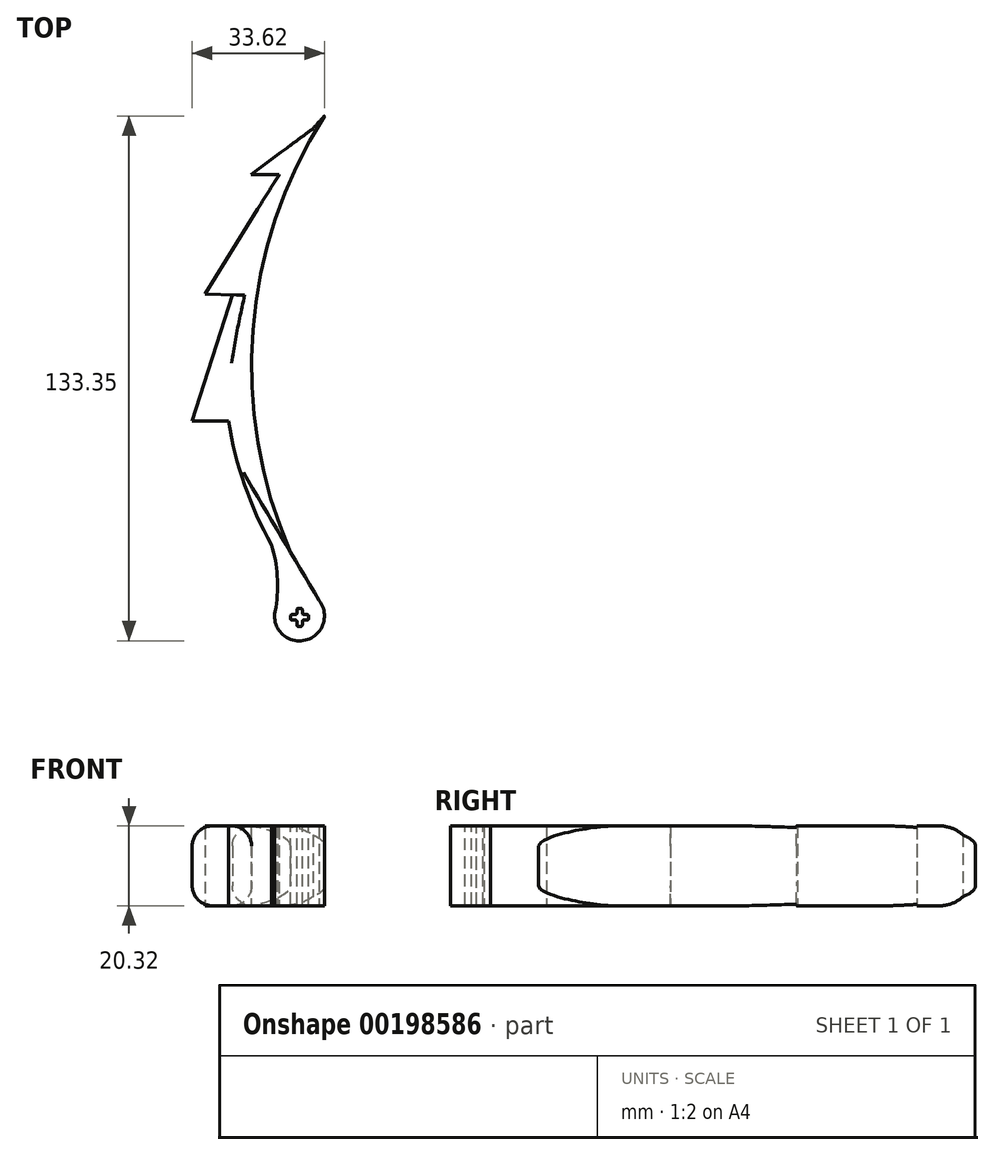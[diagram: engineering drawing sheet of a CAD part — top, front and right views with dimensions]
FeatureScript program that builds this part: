
annotation { "Feature Type Name" : "Feature", "Feature Type Description" : "" }
export const myFeature = defineFeature(function(context is Context, id is Id, definition is map)
    precondition{}
    {
        {
            var Q0;
            Q0=qCreatedBy(makeId("Top.planeOp"),FACE);
            var sketch = newSketch(context, id + "F0", { "sketchPlane" : qUnion([Q0])});
            skPoint(sketch, "E0.middle", {"position": v(0, 0) * mm});
            skPoint(sketch, "E1", {"position": v(0, -63.5) * mm});
            skArc(sketch, "E2", {"start": v(12.7, 63.5) * mm, "mid": v(11.22, 61.91) * mm, "end": v(9.78, 60.29) * mm});
            skArc(sketch, "E3", {"start": v(12.7, 63.5) * mm, "mid": v(-5.49, 9.12) * mm, "end": v(4.1, -47.41) * mm});
            skPoint(sketch, "E4", {"position": v(6.35, -63.5) * mm});
            skArc(sketch, "E5", {"start": v(0.39, -61.32) * mm, "mid": v(7.32, -69.78) * mm, "end": v(11.37, -59.62) * mm});
            skArc(sketch, "E6", {"start": v(4.1, -47.41) * mm, "mid": v(7.73, -53.52) * mm, "end": v(11.37, -59.62) * mm});
            skArc(sketch, "E7", {"start": v(0.39, -61.32) * mm, "mid": v(0.7, -53.34) * mm, "end": v(-0.69, -45.47) * mm});
            skLineSegment(sketch, "E8", {"start": v(9.78, 60.29) * mm, "end": v(-5.96, 48.67) * mm});
            skLineSegment(sketch, "E9", {"start": v(-5.96, 48.67) * mm, "end": v(1.21, 48.67) * mm});
            skLineSegment(sketch, "E10", {"start": v(1.21, 48.67) * mm, "end": v(-17.68, 18.32) * mm});
            skLineSegment(sketch, "E11", {"start": v(-17.68, 18.32) * mm, "end": v(-10.71, 18.11) * mm});
            skLineSegment(sketch, "E12", {"start": v(-10.71, 18.11) * mm, "end": v(-20.92, -14) * mm});
            skLineSegment(sketch, "E13", {"start": v(-20.92, -14) * mm, "end": v(-11.63, -14) * mm});
            skArc(sketch, "E14.trimOffspring", {"start": v(-10.9, 18.12) * mm, "mid": v(-11.05, 17.36) * mm, "end": v(-11.2, 16.6) * mm});
            skArc(sketch, "E15.trimOffspring", {"start": v(-11.63, -14) * mm, "mid": v(-7.6, -30.24) * mm, "end": v(-0.69, -45.47) * mm});
            skSolve(sketch);
        }
        {
            var Q0;
            Q0=makeQuery(id+"F0.imprint","IMPRINT",FACE,{"disambiguationData":[TD([[makeQuery(id+"F0.imprint","IMPRINT",EDGE,{"derivedFrom":sQuery(id+"F0.wireOp",EDGE,"E2")}),1.0]])]});
            extrude(context, id + "F1", {"entities" : qUnion([Q0]), "depth" : 20.32 * mm});
        }
        {
            var Q0;
            Q0=makeQuery(id+"F1.opExtrude","CAP_EDGE",EDGE,{"disambiguationData":[OSD([sQuery(id+"F0.wireOp",EDGE,"E3")])],"isStart":false});
            var Q1;
            Q1=makeQuery(id+"F1.opExtrude","CAP_EDGE",EDGE,{"disambiguationData":[OSD([sQuery(id+"F0.wireOp",EDGE,"E3")])],"isStart":true});
            var Q2;
            Q2=makeQuery(id+"F1.opExtrude","CAP_EDGE",EDGE,{"disambiguationData":[OSD([sQuery(id+"F0.wireOp",EDGE,"E12")])],"isStart":false});
            var Q3;
            Q3=makeQuery(id+"F1.opExtrude","CAP_EDGE",EDGE,{"disambiguationData":[OSD([sQuery(id+"F0.wireOp",EDGE,"E12")])],"isStart":true});
            fillet(context, id + "F2", {"entities" : qUnion([Q0, Q1, Q2, Q3]), "radius" : 5.08 * mm, "tangentPropagation" : true, "allowEdgeOverflow" : false});
        }
        {
            var Q0;
            Q0=makeQuery(id+"F2.opFillet","SPLIT",FACE,{"disambiguationData":[OD(0.0)],"derivedFrom":makeQuery(id+"F1.opExtrude","CAP_FACE",FACE,{"disambiguationData":[OSD([sQuery(id+"F0.wireOp",EDGE,"E2"),sQuery(id+"F0.wireOp",EDGE,"E3"),sQuery(id+"F0.wireOp",EDGE,"E5"),sQuery(id+"F0.wireOp",EDGE,"E6"),sQuery(id+"F0.wireOp",EDGE,"E7"),sQuery(id+"F0.wireOp",EDGE,"E8"),sQuery(id+"F0.wireOp",EDGE,"E9"),sQuery(id+"F0.wireOp",EDGE,"E10"),sQuery(id+"F0.wireOp",EDGE,"E11"),sQuery(id+"F0.wireOp",EDGE,"E12"),sQuery(id+"F0.wireOp",EDGE,"E13"),sQuery(id+"F0.wireOp",EDGE,"E15.trimOffspring")])],"isStart":false})});
            var sketch = newSketch(context, id + "F3", { "sketchPlane" : qUnion([Q0])});
            skSolve(sketch);
        }
        {
            var Q0;
            {var subQ5=sQuery(id+"F0.wireOp",EDGE,"E5");Q0=makeQuery(id+"F3.imprint","IMPRINT",FACE,{"disambiguationData":[TD([[makeQuery(id+"F3.imprint","IMPRINT",EDGE,{"derivedFrom":makeQuery(id+"F1.opExtrude","CAP_EDGE",EDGE,{"disambiguationData":[OSD([subQ5])],"isStart":false})}),1.0]])]});}
            var sketch = newSketch(context, id + "F4", { "sketchPlane" : qUnion([Q0])});
            skLineSegment(sketch, "E16", {"start": v(5.7, -61.56) * mm, "end": v(7.07, -61.56) * mm});
            skLineSegment(sketch, "E17", {"start": v(7.07, -61.56) * mm, "end": v(7.07, -63.18) * mm});
            skLineSegment(sketch, "E18", {"start": v(7.07, -63.18) * mm, "end": v(8.7, -63.18) * mm});
            skLineSegment(sketch, "E19", {"start": v(8.7, -63.18) * mm, "end": v(8.7, -64.55) * mm});
            skLineSegment(sketch, "E20", {"start": v(8.7, -64.55) * mm, "end": v(7.07, -64.55) * mm});
            skLineSegment(sketch, "E21", {"start": v(7.07, -64.55) * mm, "end": v(7.07, -66.18) * mm});
            skLineSegment(sketch, "E22", {"start": v(7.07, -66.18) * mm, "end": v(5.7, -66.18) * mm});
            skLineSegment(sketch, "E23", {"start": v(5.7, -66.18) * mm, "end": v(5.7, -64.55) * mm});
            skLineSegment(sketch, "E24", {"start": v(5.7, -64.55) * mm, "end": v(4.07, -64.55) * mm});
            skLineSegment(sketch, "E25", {"start": v(4.07, -64.55) * mm, "end": v(4.07, -63.18) * mm});
            skLineSegment(sketch, "E26", {"start": v(4.07, -63.18) * mm, "end": v(5.7, -63.18) * mm});
            skLineSegment(sketch, "E27", {"start": v(5.7, -63.18) * mm, "end": v(5.7, -61.56) * mm});
            skSolve(sketch);
        }
        {
            var Q0;
            Q0=makeQuery(id+"F4.imprint","IMPRINT",FACE,{"disambiguationData":[TD([[makeQuery(id+"F4.imprint","IMPRINT",EDGE,{"derivedFrom":sQuery(id+"F4.wireOp",EDGE,"E16")}),-1.0]])]});
            extrude(context, id + "F5", {"entities" : qUnion([Q0]), "operationType" : NewBodyOperationType.REMOVE, "oppositeDirection" : true, "depth" : 25.4 * mm});
        }
        {
            var Q0;
            Q0=makeQuery(id+"F5.boolean.opBoolean","COPY",EDGE,{"derivedFrom":makeQuery(id+"F5.opExtrude","SWEPT_EDGE",EDGE,{"disambiguationData":[OSD([sQuery(id+"F4.wireOp",EDGE,"E26"),sQuery(id+"F4.wireOp",EDGE,"E27")])]})});
            var Q1;
            Q1=makeQuery(id+"F5.boolean.opBoolean","COPY",EDGE,{"derivedFrom":makeQuery(id+"F5.opExtrude","SWEPT_EDGE",EDGE,{"disambiguationData":[OSD([sQuery(id+"F4.wireOp",EDGE,"E16"),sQuery(id+"F4.wireOp",EDGE,"E27")])]})});
            var Q2;
            Q2=makeQuery(id+"F5.boolean.opBoolean","COPY",EDGE,{"derivedFrom":makeQuery(id+"F5.opExtrude","CAP_EDGE",EDGE,{"disambiguationData":[OSD([sQuery(id+"F4.wireOp",EDGE,"E16")])],"isStart":true})});
            var Q3;
            Q3=makeQuery(id+"F5.boolean.opBoolean","COPY",EDGE,{"derivedFrom":makeQuery(id+"F5.opExtrude","CAP_EDGE",EDGE,{"disambiguationData":[OSD([sQuery(id+"F4.wireOp",EDGE,"E27")])],"isStart":true})});
            var Q4;
            Q4=makeQuery(id+"F5.boolean.opBoolean","COPY",EDGE,{"derivedFrom":makeQuery(id+"F5.opExtrude","CAP_EDGE",EDGE,{"disambiguationData":[OSD([sQuery(id+"F4.wireOp",EDGE,"E26")])],"isStart":true})});
            var Q5;
            Q5=makeQuery(id+"F5.boolean.opBoolean","COPY",EDGE,{"derivedFrom":makeQuery(id+"F5.opExtrude","CAP_EDGE",EDGE,{"disambiguationData":[OSD([sQuery(id+"F4.wireOp",EDGE,"E25")])],"isStart":true})});
            var Q6;
            Q6=makeQuery(id+"F5.boolean.opBoolean","COPY",EDGE,{"derivedFrom":makeQuery(id+"F5.opExtrude","SWEPT_EDGE",EDGE,{"disambiguationData":[OSD([sQuery(id+"F4.wireOp",EDGE,"E25"),sQuery(id+"F4.wireOp",EDGE,"E26")])]})});
            var Q7;
            Q7=makeQuery(id+"F5.boolean.opBoolean","COPY",EDGE,{"derivedFrom":makeQuery(id+"F5.opExtrude","CAP_EDGE",EDGE,{"disambiguationData":[OSD([sQuery(id+"F4.wireOp",EDGE,"E24")])],"isStart":true})});
            var Q8;
            Q8=makeQuery(id+"F5.boolean.opBoolean","COPY",EDGE,{"derivedFrom":makeQuery(id+"F5.opExtrude","CAP_EDGE",EDGE,{"disambiguationData":[OSD([sQuery(id+"F4.wireOp",EDGE,"E23")])],"isStart":true})});
            var Q9;
            Q9=makeQuery(id+"F5.boolean.opBoolean","COPY",EDGE,{"derivedFrom":makeQuery(id+"F5.opExtrude","CAP_EDGE",EDGE,{"disambiguationData":[OSD([sQuery(id+"F4.wireOp",EDGE,"E22")])],"isStart":true})});
            var Q10;
            Q10=makeQuery(id+"F5.boolean.opBoolean","COPY",EDGE,{"derivedFrom":makeQuery(id+"F5.opExtrude","CAP_EDGE",EDGE,{"disambiguationData":[OSD([sQuery(id+"F4.wireOp",EDGE,"E21")])],"isStart":true})});
            var Q11;
            Q11=makeQuery(id+"F5.boolean.opBoolean","COPY",EDGE,{"derivedFrom":makeQuery(id+"F5.opExtrude","CAP_EDGE",EDGE,{"disambiguationData":[OSD([sQuery(id+"F4.wireOp",EDGE,"E20")])],"isStart":true})});
            var Q12;
            Q12=makeQuery(id+"F5.boolean.opBoolean","COPY",EDGE,{"derivedFrom":makeQuery(id+"F5.opExtrude","CAP_EDGE",EDGE,{"disambiguationData":[OSD([sQuery(id+"F4.wireOp",EDGE,"E18")])],"isStart":true})});
            var Q13;
            Q13=makeQuery(id+"F5.boolean.opBoolean","COPY",EDGE,{"derivedFrom":makeQuery(id+"F5.opExtrude","CAP_EDGE",EDGE,{"disambiguationData":[OSD([sQuery(id+"F4.wireOp",EDGE,"E17")])],"isStart":true})});
            var Q14;
            Q14=makeQuery(id+"F5.boolean.opBoolean","COPY",EDGE,{"derivedFrom":makeQuery(id+"F5.opExtrude","CAP_EDGE",EDGE,{"disambiguationData":[OSD([sQuery(id+"F4.wireOp",EDGE,"E19")])],"isStart":true})});
            var Q15;
            Q15=makeQuery(id+"F5.boolean.opBoolean","COPY",EDGE,{"derivedFrom":makeQuery(id+"F5.opExtrude","SWEPT_EDGE",EDGE,{"disambiguationData":[OSD([sQuery(id+"F4.wireOp",EDGE,"E17"),sQuery(id+"F4.wireOp",EDGE,"E18")])]})});
            var Q16;
            Q16=makeQuery(id+"F5.boolean.opBoolean","COPY",EDGE,{"derivedFrom":makeQuery(id+"F5.opExtrude","SWEPT_EDGE",EDGE,{"disambiguationData":[OSD([sQuery(id+"F4.wireOp",EDGE,"E23"),sQuery(id+"F4.wireOp",EDGE,"E24")])]})});
            var Q17;
            Q17=makeQuery(id+"F5.boolean.opBoolean","COPY",EDGE,{"derivedFrom":makeQuery(id+"F5.opExtrude","SWEPT_EDGE",EDGE,{"disambiguationData":[OSD([sQuery(id+"F4.wireOp",EDGE,"E20"),sQuery(id+"F4.wireOp",EDGE,"E21")])]})});
            var Q18;
            Q18=makeQuery(id+"F5.boolean.opBoolean","COPY",EDGE,{"derivedFrom":makeQuery(id+"F5.opExtrude","SWEPT_EDGE",EDGE,{"disambiguationData":[OSD([sQuery(id+"F4.wireOp",EDGE,"E19"),sQuery(id+"F4.wireOp",EDGE,"E20")])]})});
            var Q19;
            Q19=makeQuery(id+"F5.boolean.opBoolean","INTERSECT",EDGE,{"derivedFrom":[makeQuery(id+"F2.opFillet","SPLIT",FACE,{"disambiguationData":[OD(0.0)],"derivedFrom":makeQuery(id+"F1.opExtrude","CAP_FACE",FACE,{"disambiguationData":[OSD([sQuery(id+"F0.wireOp",EDGE,"E2"),sQuery(id+"F0.wireOp",EDGE,"E3"),sQuery(id+"F0.wireOp",EDGE,"E5"),sQuery(id+"F0.wireOp",EDGE,"E6"),sQuery(id+"F0.wireOp",EDGE,"E7"),sQuery(id+"F0.wireOp",EDGE,"E8"),sQuery(id+"F0.wireOp",EDGE,"E9"),sQuery(id+"F0.wireOp",EDGE,"E10"),sQuery(id+"F0.wireOp",EDGE,"E11"),sQuery(id+"F0.wireOp",EDGE,"E12"),sQuery(id+"F0.wireOp",EDGE,"E13"),sQuery(id+"F0.wireOp",EDGE,"E15.trimOffspring")])],"isStart":true})}),makeQuery(id+"F5.opExtrude","SWEPT_FACE",FACE,{"disambiguationData":[OSD([sQuery(id+"F4.wireOp",EDGE,"E17")])]})]});
            var Q20;
            Q20=makeQuery(id+"F5.boolean.opBoolean","INTERSECT",EDGE,{"derivedFrom":[makeQuery(id+"F2.opFillet","SPLIT",FACE,{"disambiguationData":[OD(0.0)],"derivedFrom":makeQuery(id+"F1.opExtrude","CAP_FACE",FACE,{"disambiguationData":[OSD([sQuery(id+"F0.wireOp",EDGE,"E2"),sQuery(id+"F0.wireOp",EDGE,"E3"),sQuery(id+"F0.wireOp",EDGE,"E5"),sQuery(id+"F0.wireOp",EDGE,"E6"),sQuery(id+"F0.wireOp",EDGE,"E7"),sQuery(id+"F0.wireOp",EDGE,"E8"),sQuery(id+"F0.wireOp",EDGE,"E9"),sQuery(id+"F0.wireOp",EDGE,"E10"),sQuery(id+"F0.wireOp",EDGE,"E11"),sQuery(id+"F0.wireOp",EDGE,"E12"),sQuery(id+"F0.wireOp",EDGE,"E13"),sQuery(id+"F0.wireOp",EDGE,"E15.trimOffspring")])],"isStart":true})}),makeQuery(id+"F5.opExtrude","SWEPT_FACE",FACE,{"disambiguationData":[OSD([sQuery(id+"F4.wireOp",EDGE,"E16")])]})]});
            var Q21;
            Q21=makeQuery(id+"F5.boolean.opBoolean","INTERSECT",EDGE,{"derivedFrom":[makeQuery(id+"F2.opFillet","SPLIT",FACE,{"disambiguationData":[OD(0.0)],"derivedFrom":makeQuery(id+"F1.opExtrude","CAP_FACE",FACE,{"disambiguationData":[OSD([sQuery(id+"F0.wireOp",EDGE,"E2"),sQuery(id+"F0.wireOp",EDGE,"E3"),sQuery(id+"F0.wireOp",EDGE,"E5"),sQuery(id+"F0.wireOp",EDGE,"E6"),sQuery(id+"F0.wireOp",EDGE,"E7"),sQuery(id+"F0.wireOp",EDGE,"E8"),sQuery(id+"F0.wireOp",EDGE,"E9"),sQuery(id+"F0.wireOp",EDGE,"E10"),sQuery(id+"F0.wireOp",EDGE,"E11"),sQuery(id+"F0.wireOp",EDGE,"E12"),sQuery(id+"F0.wireOp",EDGE,"E13"),sQuery(id+"F0.wireOp",EDGE,"E15.trimOffspring")])],"isStart":true})}),makeQuery(id+"F5.opExtrude","SWEPT_FACE",FACE,{"disambiguationData":[OSD([sQuery(id+"F4.wireOp",EDGE,"E27")])]})]});
            var Q22;
            Q22=makeQuery(id+"F5.boolean.opBoolean","INTERSECT",EDGE,{"derivedFrom":[makeQuery(id+"F2.opFillet","SPLIT",FACE,{"disambiguationData":[OD(0.0)],"derivedFrom":makeQuery(id+"F1.opExtrude","CAP_FACE",FACE,{"disambiguationData":[OSD([sQuery(id+"F0.wireOp",EDGE,"E2"),sQuery(id+"F0.wireOp",EDGE,"E3"),sQuery(id+"F0.wireOp",EDGE,"E5"),sQuery(id+"F0.wireOp",EDGE,"E6"),sQuery(id+"F0.wireOp",EDGE,"E7"),sQuery(id+"F0.wireOp",EDGE,"E8"),sQuery(id+"F0.wireOp",EDGE,"E9"),sQuery(id+"F0.wireOp",EDGE,"E10"),sQuery(id+"F0.wireOp",EDGE,"E11"),sQuery(id+"F0.wireOp",EDGE,"E12"),sQuery(id+"F0.wireOp",EDGE,"E13"),sQuery(id+"F0.wireOp",EDGE,"E15.trimOffspring")])],"isStart":true})}),makeQuery(id+"F5.opExtrude","SWEPT_FACE",FACE,{"disambiguationData":[OSD([sQuery(id+"F4.wireOp",EDGE,"E25")])]})]});
            var Q23;
            Q23=makeQuery(id+"F5.boolean.opBoolean","COPY",EDGE,{"derivedFrom":makeQuery(id+"F5.opExtrude","SWEPT_EDGE",EDGE,{"disambiguationData":[OSD([sQuery(id+"F4.wireOp",EDGE,"E24"),sQuery(id+"F4.wireOp",EDGE,"E25")])]})});
            var Q24;
            Q24=makeQuery(id+"F5.boolean.opBoolean","INTERSECT",EDGE,{"derivedFrom":[makeQuery(id+"F2.opFillet","SPLIT",FACE,{"disambiguationData":[OD(0.0)],"derivedFrom":makeQuery(id+"F1.opExtrude","CAP_FACE",FACE,{"disambiguationData":[OSD([sQuery(id+"F0.wireOp",EDGE,"E2"),sQuery(id+"F0.wireOp",EDGE,"E3"),sQuery(id+"F0.wireOp",EDGE,"E5"),sQuery(id+"F0.wireOp",EDGE,"E6"),sQuery(id+"F0.wireOp",EDGE,"E7"),sQuery(id+"F0.wireOp",EDGE,"E8"),sQuery(id+"F0.wireOp",EDGE,"E9"),sQuery(id+"F0.wireOp",EDGE,"E10"),sQuery(id+"F0.wireOp",EDGE,"E11"),sQuery(id+"F0.wireOp",EDGE,"E12"),sQuery(id+"F0.wireOp",EDGE,"E13"),sQuery(id+"F0.wireOp",EDGE,"E15.trimOffspring")])],"isStart":true})}),makeQuery(id+"F5.opExtrude","SWEPT_FACE",FACE,{"disambiguationData":[OSD([sQuery(id+"F4.wireOp",EDGE,"E24")])]})]});
            var Q25;
            Q25=makeQuery(id+"F5.boolean.opBoolean","INTERSECT",EDGE,{"derivedFrom":[makeQuery(id+"F2.opFillet","SPLIT",FACE,{"disambiguationData":[OD(0.0)],"derivedFrom":makeQuery(id+"F1.opExtrude","CAP_FACE",FACE,{"disambiguationData":[OSD([sQuery(id+"F0.wireOp",EDGE,"E2"),sQuery(id+"F0.wireOp",EDGE,"E3"),sQuery(id+"F0.wireOp",EDGE,"E5"),sQuery(id+"F0.wireOp",EDGE,"E6"),sQuery(id+"F0.wireOp",EDGE,"E7"),sQuery(id+"F0.wireOp",EDGE,"E8"),sQuery(id+"F0.wireOp",EDGE,"E9"),sQuery(id+"F0.wireOp",EDGE,"E10"),sQuery(id+"F0.wireOp",EDGE,"E11"),sQuery(id+"F0.wireOp",EDGE,"E12"),sQuery(id+"F0.wireOp",EDGE,"E13"),sQuery(id+"F0.wireOp",EDGE,"E15.trimOffspring")])],"isStart":true})}),makeQuery(id+"F5.opExtrude","SWEPT_FACE",FACE,{"disambiguationData":[OSD([sQuery(id+"F4.wireOp",EDGE,"E23")])]})]});
            var Q26;
            Q26=makeQuery(id+"F5.boolean.opBoolean","INTERSECT",EDGE,{"derivedFrom":[makeQuery(id+"F2.opFillet","SPLIT",FACE,{"disambiguationData":[OD(0.0)],"derivedFrom":makeQuery(id+"F1.opExtrude","CAP_FACE",FACE,{"disambiguationData":[OSD([sQuery(id+"F0.wireOp",EDGE,"E2"),sQuery(id+"F0.wireOp",EDGE,"E3"),sQuery(id+"F0.wireOp",EDGE,"E5"),sQuery(id+"F0.wireOp",EDGE,"E6"),sQuery(id+"F0.wireOp",EDGE,"E7"),sQuery(id+"F0.wireOp",EDGE,"E8"),sQuery(id+"F0.wireOp",EDGE,"E9"),sQuery(id+"F0.wireOp",EDGE,"E10"),sQuery(id+"F0.wireOp",EDGE,"E11"),sQuery(id+"F0.wireOp",EDGE,"E12"),sQuery(id+"F0.wireOp",EDGE,"E13"),sQuery(id+"F0.wireOp",EDGE,"E15.trimOffspring")])],"isStart":true})}),makeQuery(id+"F5.opExtrude","SWEPT_FACE",FACE,{"disambiguationData":[OSD([sQuery(id+"F4.wireOp",EDGE,"E21")])]})]});
            var Q27;
            Q27=makeQuery(id+"F5.boolean.opBoolean","INTERSECT",EDGE,{"derivedFrom":[makeQuery(id+"F2.opFillet","SPLIT",FACE,{"disambiguationData":[OD(0.0)],"derivedFrom":makeQuery(id+"F1.opExtrude","CAP_FACE",FACE,{"disambiguationData":[OSD([sQuery(id+"F0.wireOp",EDGE,"E2"),sQuery(id+"F0.wireOp",EDGE,"E3"),sQuery(id+"F0.wireOp",EDGE,"E5"),sQuery(id+"F0.wireOp",EDGE,"E6"),sQuery(id+"F0.wireOp",EDGE,"E7"),sQuery(id+"F0.wireOp",EDGE,"E8"),sQuery(id+"F0.wireOp",EDGE,"E9"),sQuery(id+"F0.wireOp",EDGE,"E10"),sQuery(id+"F0.wireOp",EDGE,"E11"),sQuery(id+"F0.wireOp",EDGE,"E12"),sQuery(id+"F0.wireOp",EDGE,"E13"),sQuery(id+"F0.wireOp",EDGE,"E15.trimOffspring")])],"isStart":true})}),makeQuery(id+"F5.opExtrude","SWEPT_FACE",FACE,{"disambiguationData":[OSD([sQuery(id+"F4.wireOp",EDGE,"E22")])]})]});
            var Q28;
            Q28=makeQuery(id+"F5.boolean.opBoolean","COPY",EDGE,{"derivedFrom":makeQuery(id+"F5.opExtrude","SWEPT_EDGE",EDGE,{"disambiguationData":[OSD([sQuery(id+"F4.wireOp",EDGE,"E21"),sQuery(id+"F4.wireOp",EDGE,"E22")])]})});
            var Q29;
            Q29=makeQuery(id+"F5.boolean.opBoolean","COPY",EDGE,{"derivedFrom":makeQuery(id+"F5.opExtrude","SWEPT_EDGE",EDGE,{"disambiguationData":[OSD([sQuery(id+"F4.wireOp",EDGE,"E22"),sQuery(id+"F4.wireOp",EDGE,"E23")])]})});
            var Q30;
            Q30=makeQuery(id+"F5.boolean.opBoolean","INTERSECT",EDGE,{"derivedFrom":[makeQuery(id+"F2.opFillet","SPLIT",FACE,{"disambiguationData":[OD(0.0)],"derivedFrom":makeQuery(id+"F1.opExtrude","CAP_FACE",FACE,{"disambiguationData":[OSD([sQuery(id+"F0.wireOp",EDGE,"E2"),sQuery(id+"F0.wireOp",EDGE,"E3"),sQuery(id+"F0.wireOp",EDGE,"E5"),sQuery(id+"F0.wireOp",EDGE,"E6"),sQuery(id+"F0.wireOp",EDGE,"E7"),sQuery(id+"F0.wireOp",EDGE,"E8"),sQuery(id+"F0.wireOp",EDGE,"E9"),sQuery(id+"F0.wireOp",EDGE,"E10"),sQuery(id+"F0.wireOp",EDGE,"E11"),sQuery(id+"F0.wireOp",EDGE,"E12"),sQuery(id+"F0.wireOp",EDGE,"E13"),sQuery(id+"F0.wireOp",EDGE,"E15.trimOffspring")])],"isStart":true})}),makeQuery(id+"F5.opExtrude","SWEPT_FACE",FACE,{"disambiguationData":[OSD([sQuery(id+"F4.wireOp",EDGE,"E20")])]})]});
            var Q31;
            Q31=makeQuery(id+"F5.boolean.opBoolean","INTERSECT",EDGE,{"derivedFrom":[makeQuery(id+"F2.opFillet","SPLIT",FACE,{"disambiguationData":[OD(0.0)],"derivedFrom":makeQuery(id+"F1.opExtrude","CAP_FACE",FACE,{"disambiguationData":[OSD([sQuery(id+"F0.wireOp",EDGE,"E2"),sQuery(id+"F0.wireOp",EDGE,"E3"),sQuery(id+"F0.wireOp",EDGE,"E5"),sQuery(id+"F0.wireOp",EDGE,"E6"),sQuery(id+"F0.wireOp",EDGE,"E7"),sQuery(id+"F0.wireOp",EDGE,"E8"),sQuery(id+"F0.wireOp",EDGE,"E9"),sQuery(id+"F0.wireOp",EDGE,"E10"),sQuery(id+"F0.wireOp",EDGE,"E11"),sQuery(id+"F0.wireOp",EDGE,"E12"),sQuery(id+"F0.wireOp",EDGE,"E13"),sQuery(id+"F0.wireOp",EDGE,"E15.trimOffspring")])],"isStart":true})}),makeQuery(id+"F5.opExtrude","SWEPT_FACE",FACE,{"disambiguationData":[OSD([sQuery(id+"F4.wireOp",EDGE,"E19")])]})]});
            var Q32;
            Q32=makeQuery(id+"F5.boolean.opBoolean","INTERSECT",EDGE,{"derivedFrom":[makeQuery(id+"F2.opFillet","SPLIT",FACE,{"disambiguationData":[OD(0.0)],"derivedFrom":makeQuery(id+"F1.opExtrude","CAP_FACE",FACE,{"disambiguationData":[OSD([sQuery(id+"F0.wireOp",EDGE,"E2"),sQuery(id+"F0.wireOp",EDGE,"E3"),sQuery(id+"F0.wireOp",EDGE,"E5"),sQuery(id+"F0.wireOp",EDGE,"E6"),sQuery(id+"F0.wireOp",EDGE,"E7"),sQuery(id+"F0.wireOp",EDGE,"E8"),sQuery(id+"F0.wireOp",EDGE,"E9"),sQuery(id+"F0.wireOp",EDGE,"E10"),sQuery(id+"F0.wireOp",EDGE,"E11"),sQuery(id+"F0.wireOp",EDGE,"E12"),sQuery(id+"F0.wireOp",EDGE,"E13"),sQuery(id+"F0.wireOp",EDGE,"E15.trimOffspring")])],"isStart":true})}),makeQuery(id+"F5.opExtrude","SWEPT_FACE",FACE,{"disambiguationData":[OSD([sQuery(id+"F4.wireOp",EDGE,"E18")])]})]});
            var Q33;
            Q33=makeQuery(id+"F5.boolean.opBoolean","COPY",EDGE,{"derivedFrom":makeQuery(id+"F5.opExtrude","SWEPT_EDGE",EDGE,{"disambiguationData":[OSD([sQuery(id+"F4.wireOp",EDGE,"E18"),sQuery(id+"F4.wireOp",EDGE,"E19")])]})});
            var Q34;
            Q34=makeQuery(id+"F5.boolean.opBoolean","COPY",EDGE,{"derivedFrom":makeQuery(id+"F5.opExtrude","SWEPT_EDGE",EDGE,{"disambiguationData":[OSD([sQuery(id+"F4.wireOp",EDGE,"E16"),sQuery(id+"F4.wireOp",EDGE,"E17")])]})});
            fillet(context, id + "F6", {"entities" : qUnion([Q0, Q1, Q2, Q3, Q4, Q5, Q6, Q7, Q8, Q9, Q10, Q11, Q12, Q13, Q14, Q15, Q16, Q17, Q18, Q19, Q20, Q21, Q22, Q23, Q24, Q25, Q26, Q27, Q28, Q29, Q30, Q31, Q32, Q33, Q34]), "radius" : 0.38 * mm, "tangentPropagation" : true, "allowEdgeOverflow" : false});
        }
    });
